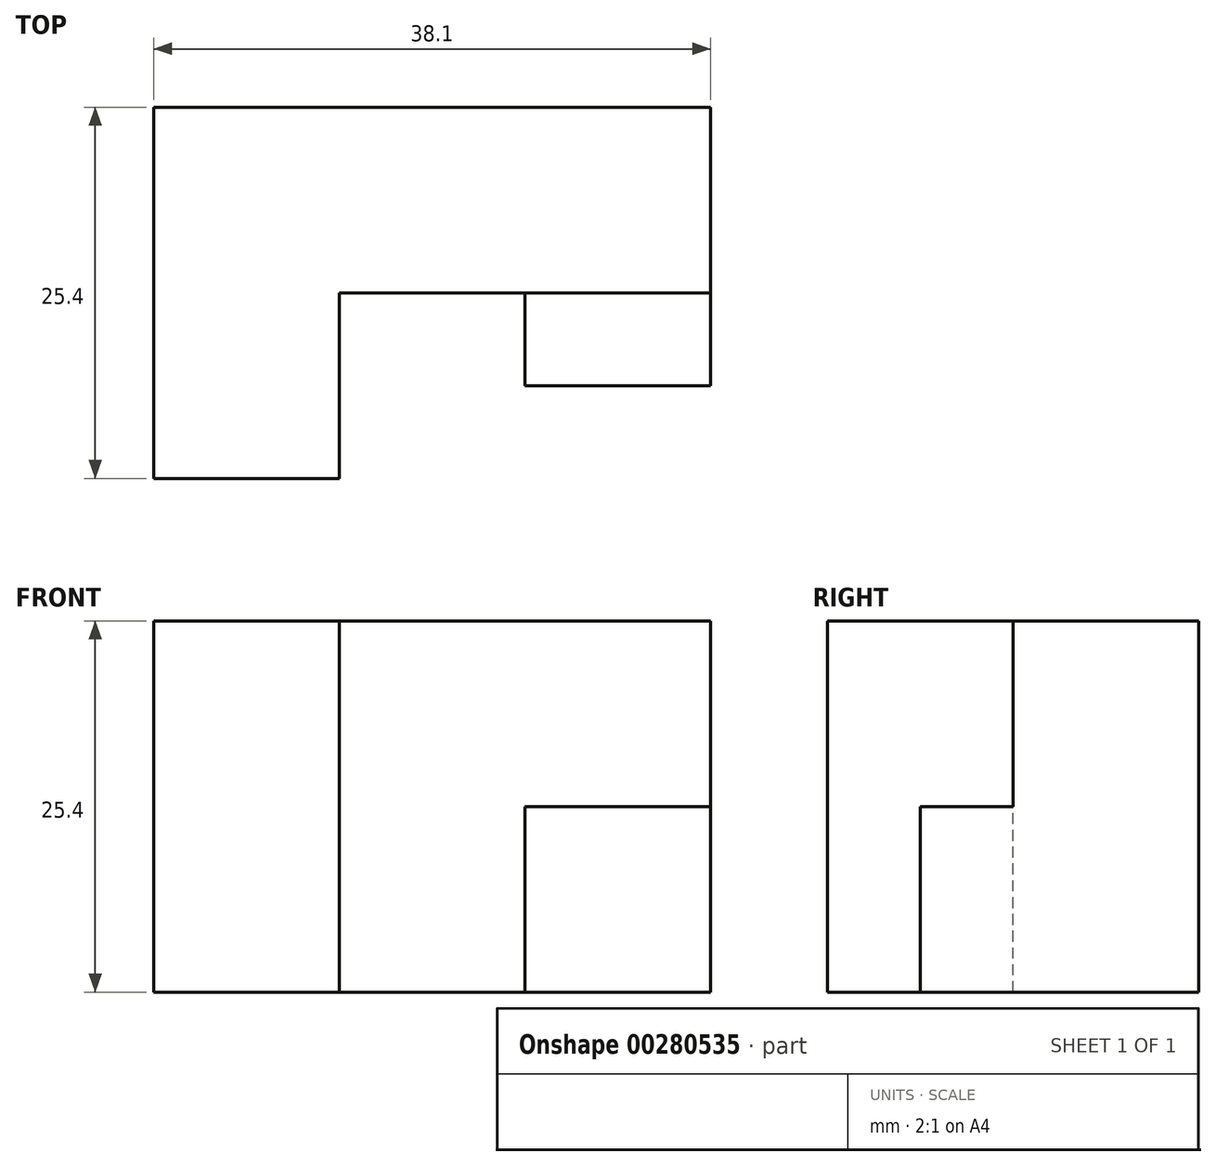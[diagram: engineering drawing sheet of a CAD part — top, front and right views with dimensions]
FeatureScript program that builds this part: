
annotation { "Feature Type Name" : "Feature", "Feature Type Description" : "" }
export const myFeature = defineFeature(function(context is Context, id is Id, definition is map)
    precondition{}
    {
        {
            var Q0;
            Q0=qCreatedBy(makeId("Right.planeOp"),FACE);
            var sketch = newSketch(context, id + "F0", { "sketchPlane" : qUnion([Q0])});
            skLineSegment(sketch, "E0.bottom", {"start": v(0, 0) * mm, "end": v(-25.4, 0) * mm});
            skLineSegment(sketch, "E0.top", {"start": v(0, 25.4) * mm, "end": v(-25.4, 25.4) * mm});
            skLineSegment(sketch, "E0.left", {"start": v(0, 0) * mm, "end": v(0, 25.4) * mm});
            skLineSegment(sketch, "E0.right", {"start": v(-25.4, 0) * mm, "end": v(-25.4, 25.4) * mm});
            skSolve(sketch);
        }
        {
            var Q0;
            Q0 = qSketchRegion(id + "F0", true);
            extrude(context, id + "F1", {"entities" : qUnion([Q0]), "depth" : 12.7 * mm});
        }
        {
            var Q0;
            Q0=makeQuery(id+"F1.opExtrude","CAP_FACE",FACE,{"disambiguationData":[OSD([sQuery(id+"F0.wireOp",EDGE,"E0.bottom"),sQuery(id+"F0.wireOp",EDGE,"E0.top"),sQuery(id+"F0.wireOp",EDGE,"E0.left"),sQuery(id+"F0.wireOp",EDGE,"E0.right")])],"isStart":false});
            var sketch = newSketch(context, id + "F2", { "sketchPlane" : qUnion([Q0])});
            skLineSegment(sketch, "E1.bottom", {"start": v(0, 0) * mm, "end": v(-12.7, 0) * mm});
            skLineSegment(sketch, "E1.top", {"start": v(0, 25.4) * mm, "end": v(-12.7, 25.4) * mm});
            skLineSegment(sketch, "E1.left", {"start": v(0, 0) * mm, "end": v(0, 25.4) * mm});
            skLineSegment(sketch, "E1.right", {"start": v(-12.7, 0) * mm, "end": v(-12.7, 25.4) * mm});
            skSolve(sketch);
        }
        {
            var Q0;
            Q0=makeQuery(id+"F2.imprint","IMPRINT",FACE,{"disambiguationData":[TD([[makeQuery(id+"F2.imprint","IMPRINT",EDGE,{"derivedFrom":sQuery(id+"F2.wireOp",EDGE,"E1.bottom")}),-1.0]])]});
            extrude(context, id + "F3", {"entities" : qUnion([Q0]), "operationType" : NewBodyOperationType.ADD, "depth" : 25.4 * mm});
        }
        {
            var Q0;
            Q0=makeQuery(id+"F3.opExtrude","SWEPT_FACE",FACE,{"disambiguationData":[OSD([sQuery(id+"F2.wireOp",EDGE,"E1.right")])]});
            var sketch = newSketch(context, id + "F4", { "sketchPlane" : qUnion([Q0])});
            skPoint(sketch, "E2.oppositeSnap0", {"position": v(12.7, 12.7) * mm});
            skPoint(sketch, "E2.oppositeSnap1", {"position": v(25.4, 25.4) * mm});
            skLineSegment(sketch, "E2.bottom", {"start": v(38.1, 0) * mm, "end": v(25.4, 0) * mm});
            skLineSegment(sketch, "E2.top", {"start": v(38.1, 12.7) * mm, "end": v(25.4, 12.7) * mm});
            skLineSegment(sketch, "E2.left", {"start": v(38.1, 0) * mm, "end": v(38.1, 12.7) * mm});
            skLineSegment(sketch, "E2.right", {"start": v(25.4, 0) * mm, "end": v(25.4, 12.7) * mm});
            skSolve(sketch);
        }
        {
            var Q0;
            Q0=makeQuery(id+"F4.imprint","IMPRINT",FACE,{"disambiguationData":[TD([[makeQuery(id+"F4.imprint","IMPRINT",EDGE,{"derivedFrom":sQuery(id+"F4.wireOp",EDGE,"E2.bottom")}),-1.0]])]});
            extrude(context, id + "F5", {"entities" : qUnion([Q0]), "operationType" : NewBodyOperationType.ADD, "depth" : 6.35 * mm});
        }
    });
